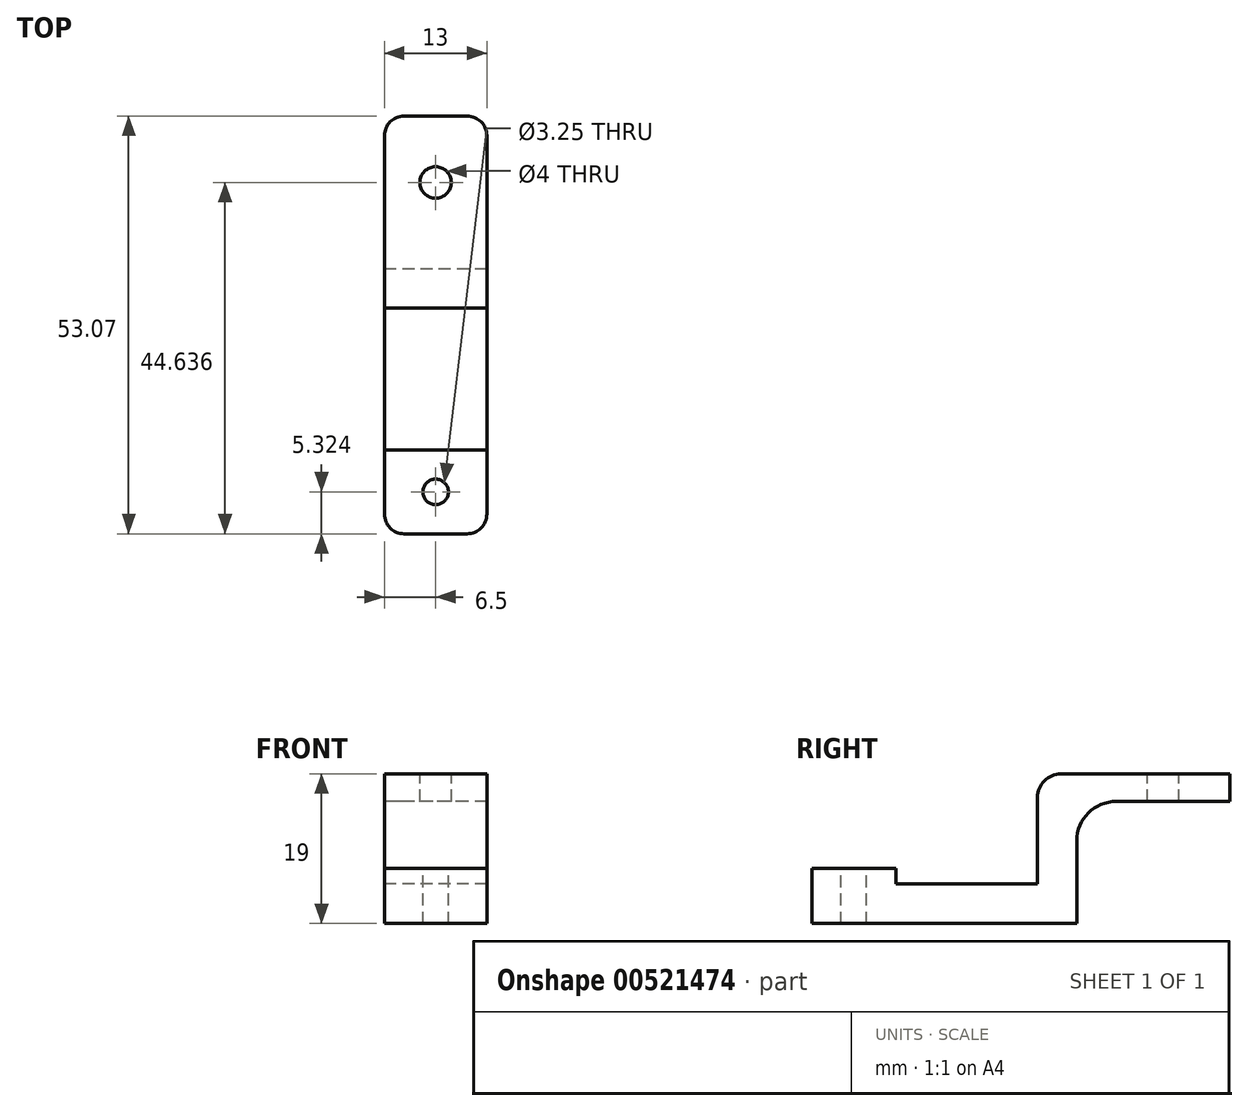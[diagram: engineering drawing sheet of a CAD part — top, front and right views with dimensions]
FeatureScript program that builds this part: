
annotation { "Feature Type Name" : "Feature", "Feature Type Description" : "" }
export const myFeature = defineFeature(function(context is Context, id is Id, definition is map)
    precondition{}
    {
        {
            var Q0;
            Q0=qCreatedBy(makeId("Right.planeOp"),FACE);
            var sketch = newSketch(context, id + "F0", { "sketchPlane" : qUnion([Q0])});
            skLineSegment(sketch, "E0", {"start": v(0, 0) * mm, "end": v(0, -7) * mm});
            skLineSegment(sketch, "E1", {"start": v(0, -7) * mm, "end": v(33.65, -7) * mm});
            skLineSegment(sketch, "E2", {"start": v(33.65, -7) * mm, "end": v(33.65, 8.5) * mm});
            skLineSegment(sketch, "E3", {"start": v(33.65, 8.5) * mm, "end": v(53.07, 8.5) * mm});
            skLineSegment(sketch, "E4", {"start": v(53.07, 8.5) * mm, "end": v(53.07, 12) * mm});
            skLineSegment(sketch, "E5", {"start": v(53.07, 12) * mm, "end": v(28.65, 12) * mm});
            skLineSegment(sketch, "E6", {"start": v(28.65, 12) * mm, "end": v(28.65, -2) * mm});
            skLineSegment(sketch, "E7", {"start": v(28.65, -2) * mm, "end": v(10.65, -2) * mm});
            skLineSegment(sketch, "E8", {"start": v(10.65, -2) * mm, "end": v(10.65, 0) * mm});
            skLineSegment(sketch, "E9", {"start": v(10.65, 0) * mm, "end": v(0, 0) * mm});
            skSolve(sketch);
        }
        {
            var Q0;
            Q0=makeQuery(id+"F0.imprint","IMPRINT",FACE,{"disambiguationData":[TD([[makeQuery(id+"F0.imprint","IMPRINT",EDGE,{"derivedFrom":sQuery(id+"F0.wireOp",EDGE,"E0")}),1.0]])]});
            extrude(context, id + "F1", {"entities" : qUnion([Q0]), "depth" : 13 * mm, "offsetDistance" : 25 * mm});
        }
        {
            var Q0;
            Q0=makeQuery(id+"F1.opExtrude","SWEPT_FACE",FACE,{"disambiguationData":[OSD([sQuery(id+"F0.wireOp",EDGE,"E9")])]});
            var sketch = newSketch(context, id + "F2", { "sketchPlane" : qUnion([Q0])});
            skCircle(sketch, "E10", {"center": v(6.5, 5.32) * mm, "radius": 1.63 * mm});
            skPoint(sketch, "E10.centerSnap0", {"position": v(0, 5.32) * mm});
            skPoint(sketch, "E11", {"position": v(6.5, 0) * mm});
            skSolve(sketch);
        }
        {
            var Q0;
            Q0=makeQuery(id+"F2.imprint","IMPRINT",FACE,{"disambiguationData":[TD([[makeQuery(id+"F2.imprint","IMPRINT",EDGE,{"derivedFrom":sQuery(id+"F2.wireOp",EDGE,"E10")}),1.0]])]});
            extrude(context, id + "F3", {"entities" : qUnion([Q0]), "operationType" : NewBodyOperationType.REMOVE, "oppositeDirection" : true, "depth" : 25 * mm, "offsetDistance" : 25 * mm});
        }
        {
            var Q0;
            Q0=makeQuery(id+"F1.opExtrude","SWEPT_FACE",FACE,{"disambiguationData":[OSD([sQuery(id+"F0.wireOp",EDGE,"E5")])]});
            var sketch = newSketch(context, id + "F4", { "sketchPlane" : qUnion([Q0])});
            skCircle(sketch, "E12", {"center": v(6.5, 44.64) * mm, "radius": 2 * mm});
            skPoint(sketch, "E12.centerSnap0", {"position": v(6.5, 53.07) * mm});
            skSolve(sketch);
        }
        {
            var Q0;
            Q0=makeQuery(id+"F4.imprint","IMPRINT",FACE,{"disambiguationData":[TD([[makeQuery(id+"F4.imprint","IMPRINT",EDGE,{"derivedFrom":sQuery(id+"F4.wireOp",EDGE,"E12")}),1.0]])]});
            extrude(context, id + "F5", {"entities" : qUnion([Q0]), "operationType" : NewBodyOperationType.REMOVE, "oppositeDirection" : true, "depth" : 25 * mm, "offsetDistance" : 25 * mm});
        }
        {
            var Q0;
            Q0=makeQuery(id+"F1.opExtrude","SWEPT_EDGE",EDGE,{"disambiguationData":[OSD([sQuery(id+"F0.wireOp",EDGE,"E2"),sQuery(id+"F0.wireOp",EDGE,"E3")])]});
            fillet(context, id + "F6", {"entities" : qUnion([Q0]), "radius" : 5 * mm, "tangentPropagation" : true, "allowEdgeOverflow" : false});
        }
        {
            var Q0;
            Q0=makeQuery(id+"F1.opExtrude","SWEPT_EDGE",EDGE,{"disambiguationData":[OSD([sQuery(id+"F0.wireOp",EDGE,"E5"),sQuery(id+"F0.wireOp",EDGE,"E6")])]});
            fillet(context, id + "F7", {"entities" : qUnion([Q0]), "radius" : 3 * mm, "tangentPropagation" : true, "allowEdgeOverflow" : false});
        }
        {
            var Q0;
            Q0=makeQuery(id+"F1.opExtrude","CAP_EDGE",EDGE,{"disambiguationData":[OSD([sQuery(id+"F0.wireOp",EDGE,"E4")])],"isStart":false});
            var Q1;
            Q1=makeQuery(id+"F1.opExtrude","CAP_EDGE",EDGE,{"disambiguationData":[OSD([sQuery(id+"F0.wireOp",EDGE,"E4")])],"isStart":true});
            var Q2;
            Q2=makeQuery(id+"F1.opExtrude","CAP_EDGE",EDGE,{"disambiguationData":[OSD([sQuery(id+"F0.wireOp",EDGE,"E0")])],"isStart":false});
            var Q3;
            Q3=makeQuery(id+"F1.opExtrude","CAP_EDGE",EDGE,{"disambiguationData":[OSD([sQuery(id+"F0.wireOp",EDGE,"E0")])],"isStart":true});
            fillet(context, id + "F8", {"entities" : qUnion([Q0, Q1, Q2, Q3]), "radius" : 2.5 * mm, "tangentPropagation" : true, "allowEdgeOverflow" : false});
        }
    });
